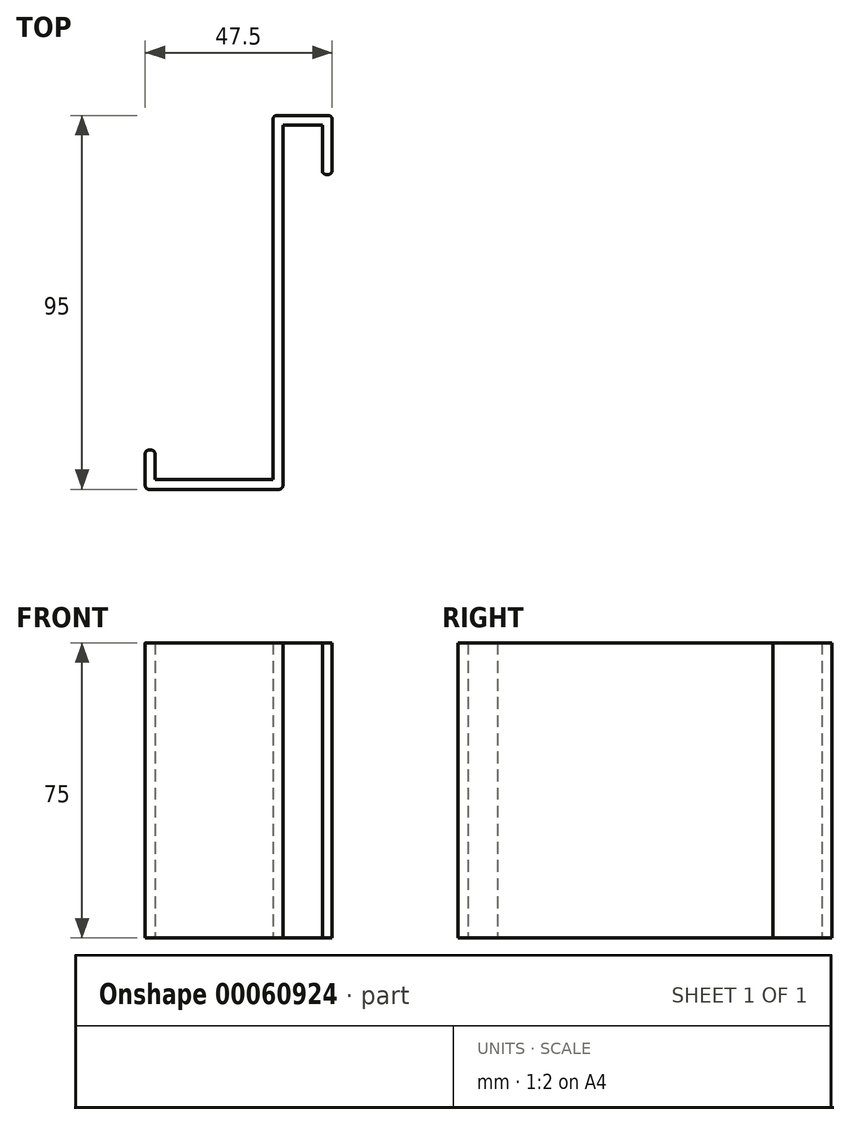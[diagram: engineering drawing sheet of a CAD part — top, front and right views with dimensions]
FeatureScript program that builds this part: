
annotation { "Feature Type Name" : "Feature", "Feature Type Description" : "" }
export const myFeature = defineFeature(function(context is Context, id is Id, definition is map)
    precondition{}
    {
        {
            var Q0;
            Q0=qCreatedBy(makeId("Top.planeOp"),FACE);
            var sketch = newSketch(context, id + "F0", { "sketchPlane" : qUnion([Q0])});
            skLineSegment(sketch, "E0", {"start": v(15, 22.03) * mm, "end": v(15, 37.03) * mm});
            skLineSegment(sketch, "E1", {"start": v(15, 37.03) * mm, "end": v(0, 37.03) * mm});
            skLineSegment(sketch, "E2", {"start": v(0, 37.03) * mm, "end": v(0, -55.47) * mm});
            skLineSegment(sketch, "E3", {"start": v(0, -55.47) * mm, "end": v(-30, -55.47) * mm});
            skLineSegment(sketch, "E4", {"start": v(-30, -55.47) * mm, "end": v(-30, -47.97) * mm});
            skLineSegment(sketch, "E5", {"start": v(-30, -47.97) * mm, "end": v(-32.5, -47.97) * mm});
            skLineSegment(sketch, "E6", {"start": v(-32.5, -47.97) * mm, "end": v(-32.5, -57.97) * mm});
            skLineSegment(sketch, "E7", {"start": v(-32.5, -57.97) * mm, "end": v(2.5, -57.97) * mm});
            skLineSegment(sketch, "E8", {"start": v(2.5, -57.97) * mm, "end": v(2.5, 34.53) * mm});
            skLineSegment(sketch, "E9", {"start": v(2.5, 34.53) * mm, "end": v(12.5, 34.53) * mm});
            skLineSegment(sketch, "E10", {"start": v(12.5, 34.53) * mm, "end": v(12.5, 22.03) * mm});
            skLineSegment(sketch, "E11", {"start": v(12.5, 22.03) * mm, "end": v(15, 22.03) * mm});
            skLineSegment(sketch, "E12", {"start": v(7.5, 37.03) * mm, "end": v(7.5, 34.53) * mm});
            skLineSegment(sketch, "E13", {"start": v(-15, -55.47) * mm, "end": v(-15, -57.97) * mm});
            skLineSegment(sketch, "E14", {"start": v(0, 0) * mm, "end": v(2.5, 0) * mm});
            skLineSegment(sketch, "E15", {"start": v(12.5, 28.28) * mm, "end": v(15, 28.28) * mm});
            skLineSegment(sketch, "E16", {"start": v(-32.5, -4.22) * mm, "end": v(-30, -4.22) * mm});
            skSolve(sketch);
        }
        {
            var Q0;
            {var subQ7=sQuery(id+"F0.wireOp",EDGE,"E13");Q0=makeQuery(id+"F0.imprint","IMPRINT",FACE,{"disambiguationData":[TD([[makeQuery(id+"F0.imprint","IMPRINT",EDGE,{"derivedFrom":subQ7}),1.0]])]});}
            var Q1;
            {var subQ3=sQuery(id+"F0.wireOp",EDGE,"E12");Q1=makeQuery(id+"F0.imprint","IMPRINT",FACE,{"disambiguationData":[TD([[makeQuery(id+"F0.imprint","IMPRINT",EDGE,{"derivedFrom":subQ3}),-1.0]])]});}
            var Q2;
            {var subQ4=sQuery(id+"F0.wireOp",EDGE,"E12");Q2=makeQuery(id+"F0.imprint","IMPRINT",FACE,{"disambiguationData":[TD([[makeQuery(id+"F0.imprint","IMPRINT",EDGE,{"derivedFrom":subQ4}),1.0]])]});}
            var Q3;
            {var subQ0=sQuery(id+"F0.wireOp",EDGE,"E11");Q3=makeQuery(id+"F0.imprint","IMPRINT",FACE,{"disambiguationData":[TD([[makeQuery(id+"F0.imprint","IMPRINT",EDGE,{"derivedFrom":subQ0}),1.0]])]});}
            var Q4;
            {var subQ1=sQuery(id+"F0.wireOp",EDGE,"E4");Q4=makeQuery(id+"F0.imprint","IMPRINT",FACE,{"disambiguationData":[TD([[makeQuery(id+"F0.imprint","IMPRINT",EDGE,{"derivedFrom":subQ1}),1.0]])]});}
            extrude(context, id + "F1", {"entities" : qUnion([Q0, Q1, Q2, Q3, Q4]), "depth" : 75 * mm});
        }
        {
            var Q0;
            Q0=makeQuery(id+"F1.opExtrude","SWEPT_EDGE",EDGE,{"disambiguationData":[OSD([sQuery(id+"F0.wireOp",EDGE,"E6"),sQuery(id+"F0.wireOp",EDGE,"E7")])]});
            var Q1;
            Q1=makeQuery(id+"F1.opExtrude","SWEPT_EDGE",EDGE,{"disambiguationData":[OSD([sQuery(id+"F0.wireOp",EDGE,"E7"),sQuery(id+"F0.wireOp",EDGE,"E8")])]});
            var Q2;
            Q2=makeQuery(id+"F1.opExtrude","SWEPT_EDGE",EDGE,{"disambiguationData":[OSD([sQuery(id+"F0.wireOp",EDGE,"E0"),sQuery(id+"F0.wireOp",EDGE,"E1")])]});
            var Q3;
            Q3=makeQuery(id+"F1.opExtrude","SWEPT_EDGE",EDGE,{"disambiguationData":[OSD([sQuery(id+"F0.wireOp",EDGE,"E1"),sQuery(id+"F0.wireOp",EDGE,"E2")])]});
            fillet(context, id + "F2", {"entities" : qUnion([Q0, Q1, Q2, Q3]), "radius" : 1 * mm, "tangentPropagation" : true, "allowEdgeOverflow" : false});
        }
        {
            var Q0;
            Q0=makeQuery(id+"F1.opExtrude","SWEPT_EDGE",EDGE,{"disambiguationData":[OSD([sQuery(id+"F0.wireOp",EDGE,"E4"),sQuery(id+"F0.wireOp",EDGE,"E5")])]});
            var Q1;
            Q1=makeQuery(id+"F1.opExtrude","SWEPT_EDGE",EDGE,{"disambiguationData":[OSD([sQuery(id+"F0.wireOp",EDGE,"E5"),sQuery(id+"F0.wireOp",EDGE,"E6")])]});
            var Q2;
            Q2=makeQuery(id+"F1.opExtrude","SWEPT_EDGE",EDGE,{"disambiguationData":[OSD([sQuery(id+"F0.wireOp",EDGE,"E0"),sQuery(id+"F0.wireOp",EDGE,"E11")])]});
            var Q3;
            Q3=makeQuery(id+"F1.opExtrude","SWEPT_EDGE",EDGE,{"disambiguationData":[OSD([sQuery(id+"F0.wireOp",EDGE,"E10"),sQuery(id+"F0.wireOp",EDGE,"E11")])]});
            fillet(context, id + "F3", {"entities" : qUnion([Q0, Q1, Q2, Q3]), "radius" : 1 * mm, "tangentPropagation" : true, "allowEdgeOverflow" : false});
        }
    });
